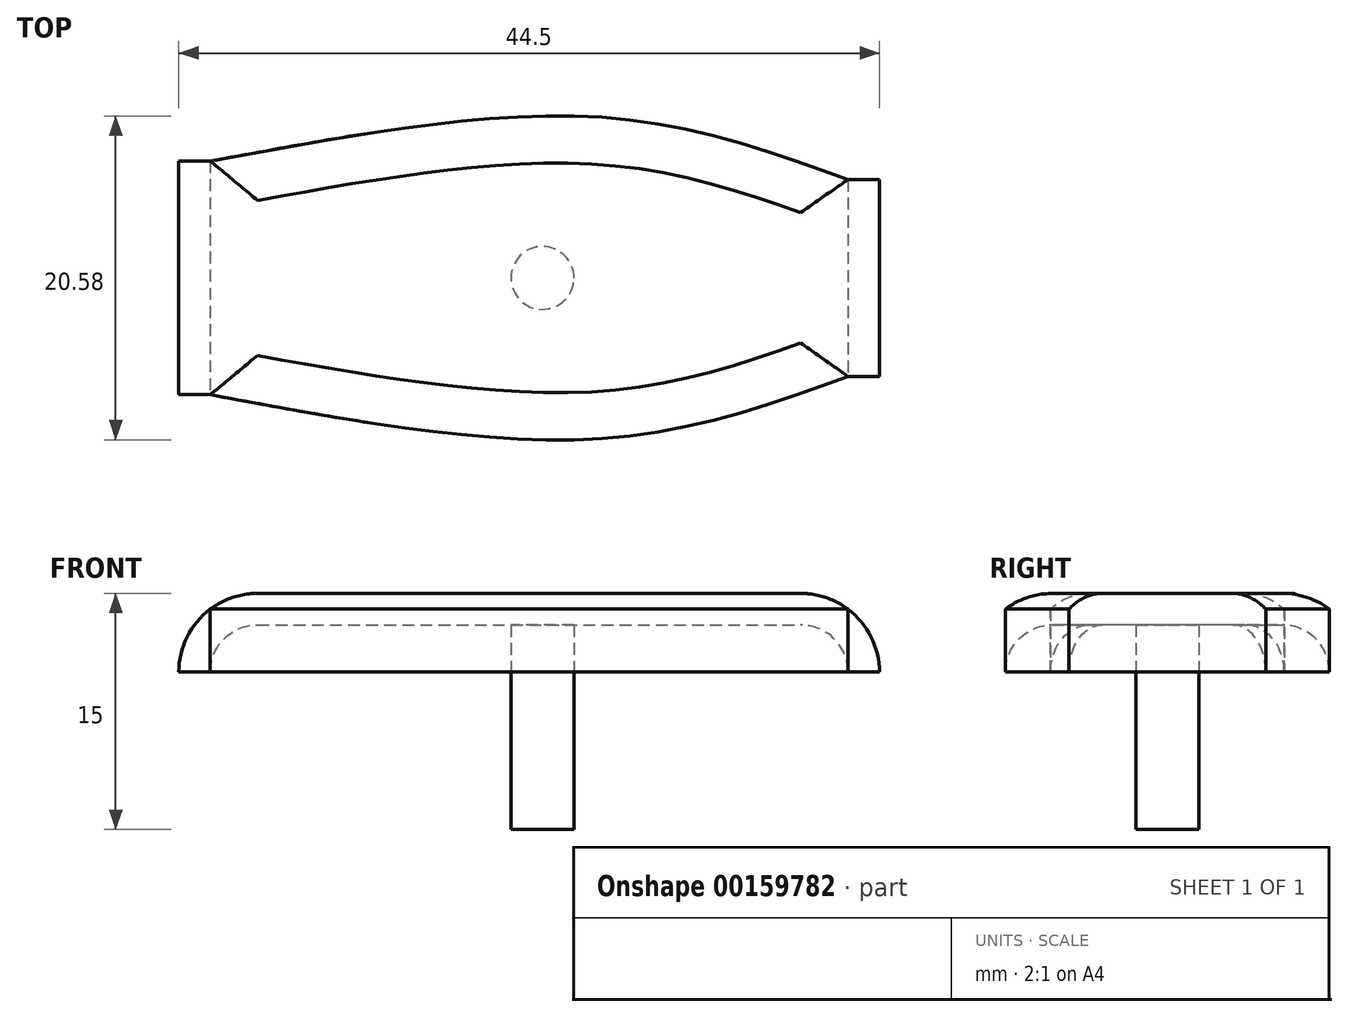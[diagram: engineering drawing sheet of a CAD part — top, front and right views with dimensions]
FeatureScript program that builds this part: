
annotation { "Feature Type Name" : "Feature", "Feature Type Description" : "" }
export const myFeature = defineFeature(function(context is Context, id is Id, definition is map)
    precondition{}
    {
        {
            var Q0;
            Q0=qCreatedBy(makeId("Top.planeOp"),FACE);
            var sketch = newSketch(context, id + "F0", { "sketchPlane" : qUnion([Q0])});
            skLineSegment(sketch, "E0.bottom", {"start": v(-20.25, -10.2) * mm, "end": v(20.25, -10.2) * mm, "construction": true});
            skLineSegment(sketch, "E0.top", {"start": v(-20.25, 10.2) * mm, "end": v(20.25, 10.2) * mm, "construction": true});
            skLineSegment(sketch, "E0.left", {"start": v(-20.25, -10.2) * mm, "end": v(-20.25, 10.2) * mm, "construction": true});
            skLineSegment(sketch, "E0.right", {"start": v(20.25, -10.2) * mm, "end": v(20.25, 10.2) * mm, "construction": true});
            skPoint(sketch, "E0.middle", {"position": v(0, 0) * mm});
            skLineSegment(sketch, "E1", {"start": v(4.65, -10.2) * mm, "end": v(4.65, 10.2) * mm, "construction": true});
            skLineSegment(sketch, "E2", {"start": v(-34.33, 0) * mm, "end": v(0, 0) * mm, "construction": true});
            skLineSegment(sketch, "E3", {"start": v(0, 0) * mm, "end": v(0, 24.06) * mm, "construction": true});
            skLineSegment(sketch, "E4", {"start": v(20.25, 6.25) * mm, "end": v(20.25, -6.25) * mm});
            skLineSegment(sketch, "E5.MirrorCS", {"start": v(84.7, 0) * mm, "end": v(50.37, 0) * mm, "construction": true});
            skLineSegment(sketch, "E6", {"start": v(-20.25, 7.42) * mm, "end": v(-20.25, -7.42) * mm});
            skFitSpline(sketch, "E7", {"points": [v(-20.25, -7.42) * mm, v(4.65, -10.2) * mm, v(20.25, -6.25) * mm], "startDerivative": vector(47.57, -8.87) * mm, "endDerivative": vector(32.89, 11.97) * mm});
            skFitSpline(sketch, "E8.MirrorCS", {"points": [v(-20.25, 7.42) * mm, v(4.65, 10.2) * mm, v(20.25, 6.25) * mm], "startDerivative": vector(47.57, 8.87) * mm, "endDerivative": vector(32.89, -11.97) * mm});
            skLineSegment(sketch, "E9", {"start": v(-20.25, 14.06) * mm, "end": v(0.85, 14.06) * mm, "construction": true});
            skCircle(sketch, "E10", {"center": v(0.85, 0) * mm, "radius": 2 * mm});
            skSolve(sketch);
        }
        {
            var Q0;
            Q0=makeQuery(id+"F0.imprint","IMPRINT",FACE,{"disambiguationData":[TD([[makeQuery(id+"F0.imprint","IMPRINT",EDGE,{"derivedFrom":sQuery(id+"F0.wireOp",EDGE,"E4")}),-1.0]])]});
            extrude(context, id + "F1", {"entities" : qUnion([Q0]), "depth" : 13 * mm});
        }
        {
            var Q0;
            Q0=makeQuery(id+"F1.opExtrude","CAP_EDGE",EDGE,{"disambiguationData":[OSD([sQuery(id+"F0.wireOp",EDGE,"E7")])],"isStart":false});
            var Q1;
            Q1=makeQuery(id+"F1.opExtrude","CAP_EDGE",EDGE,{"disambiguationData":[OSD([sQuery(id+"F0.wireOp",EDGE,"E8.MirrorCS")])],"isStart":false});
            var Q2;
            Q2=makeQuery(id+"F1.opExtrude","CAP_EDGE",EDGE,{"disambiguationData":[OSD([sQuery(id+"F0.wireOp",EDGE,"E4")])],"isStart":false});
            var Q3;
            Q3=makeQuery(id+"F1.opExtrude","CAP_EDGE",EDGE,{"disambiguationData":[OSD([sQuery(id+"F0.wireOp",EDGE,"E6")])],"isStart":false});
            fillet(context, id + "F2", {"entities" : qUnion([Q0, Q1, Q2, Q3]), "radius" : 3 * mm, "tangentPropagation" : true, "allowEdgeOverflow" : false});
        }
        {
            var Q0;
            Q0=makeQuery(id+"F1.opExtrude","CAP_FACE",FACE,{"disambiguationData":[OSD([sQuery(id+"F0.wireOp",EDGE,"E4"),sQuery(id+"F0.wireOp",EDGE,"E6"),sQuery(id+"F0.wireOp",EDGE,"E7"),sQuery(id+"F0.wireOp",EDGE,"E8.MirrorCS")])],"isStart":true});
            shell(context, id + "F3", {"entities" : qUnion([Q0]), "thickness" : 2 * mm, "oppositeDirection" : true});
        }
        {
            var Q0;
            {var subQ0=sQuery(id+"F0.wireOp",EDGE,"E4");Q0=makeQuery(id+"F3.opShell","OFFSET_FACE",FACE,{"disambiguationData":[OSD([subQ0]),TDD([makeQuery(id+"F1.opExtrude","SWEPT_FACE",FACE,{"disambiguationData":[OSD([subQ0])]})])]});}
            extrude(context, id + "F4", {"entities" : qUnion([Q0]), "operationType" : NewBodyOperationType.REMOVE, "oppositeDirection" : true, "depth" : 25 * mm});
        }
        {
            var Q0;
            {var subQ0=sQuery(id+"F0.wireOp",EDGE,"E6");Q0=makeQuery(id+"F3.opShell","OFFSET_FACE",FACE,{"disambiguationData":[OSD([subQ0]),TDD([makeQuery(id+"F1.opExtrude","SWEPT_FACE",FACE,{"disambiguationData":[OSD([subQ0])]})])]});}
            extrude(context, id + "F5", {"entities" : qUnion([Q0]), "operationType" : NewBodyOperationType.REMOVE, "oppositeDirection" : true, "depth" : 25 * mm});
        }
        {
            var Q0;
            Q0=makeQuery(id+"F1.opExtrude","CAP_FACE",FACE,{"disambiguationData":[OSD([sQuery(id+"F0.wireOp",EDGE,"E4"),sQuery(id+"F0.wireOp",EDGE,"E6"),sQuery(id+"F0.wireOp",EDGE,"E7"),sQuery(id+"F0.wireOp",EDGE,"E8.MirrorCS"),sQuery(id+"F0.wireOp",EDGE,"E10")])],"isStart":true});
            extrude(context, id + "F6", {"entities" : qUnion([Q0]), "operationType" : NewBodyOperationType.REMOVE, "oppositeDirection" : true, "depth" : 25 * mm});
        }
    });
